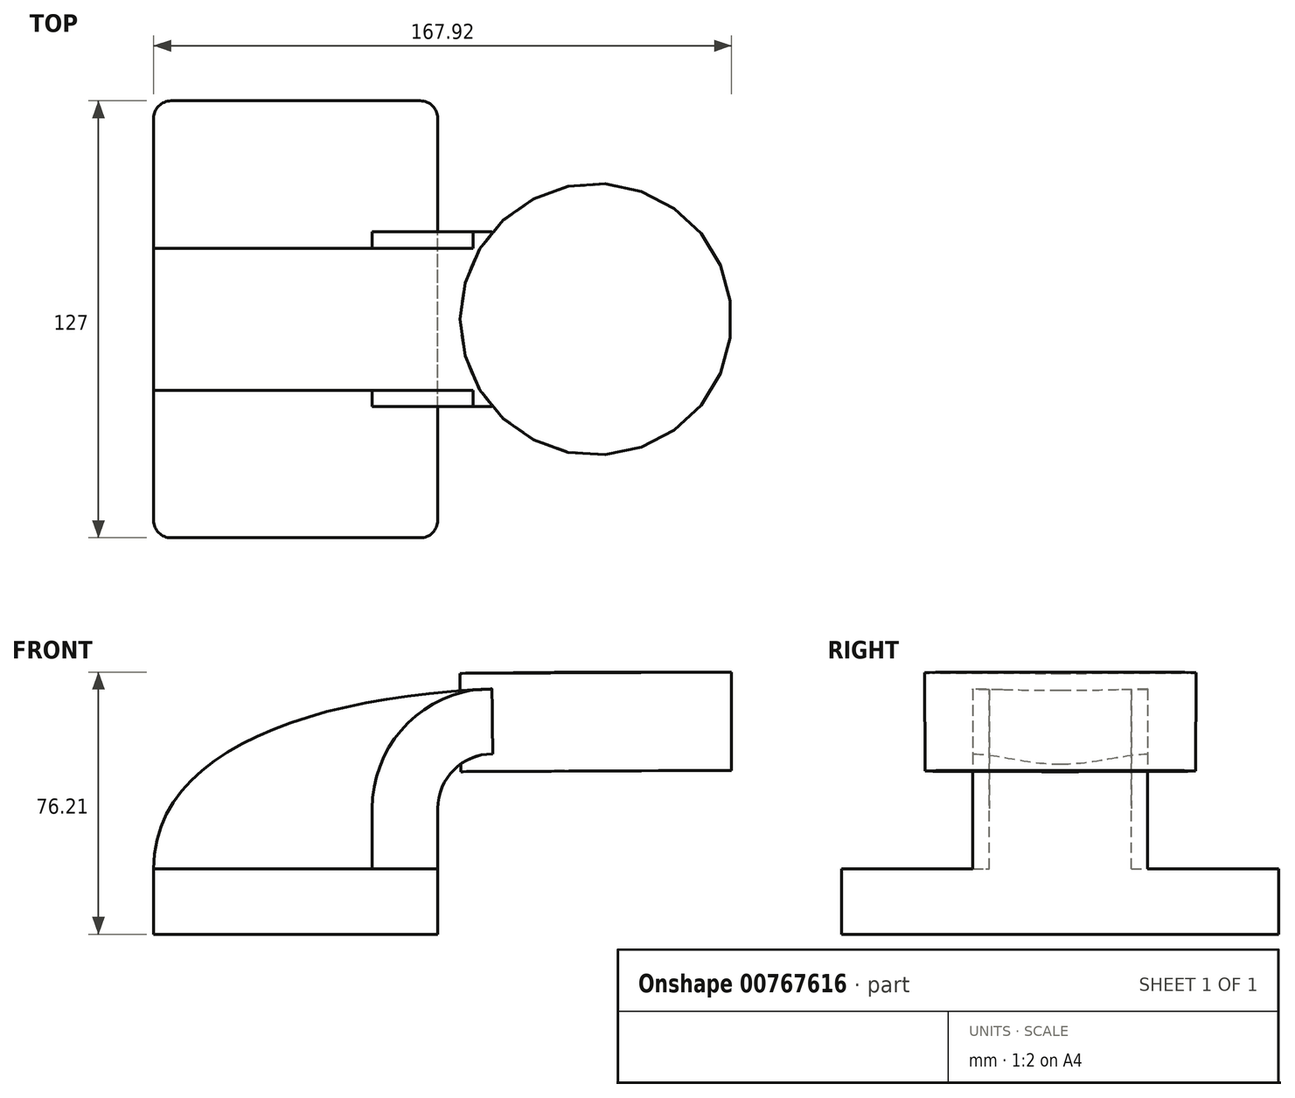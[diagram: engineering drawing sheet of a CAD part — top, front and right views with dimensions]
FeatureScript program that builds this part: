
annotation { "Feature Type Name" : "Feature", "Feature Type Description" : "" }
export const myFeature = defineFeature(function(context is Context, id is Id, definition is map)
    precondition{}
    {
        {
            var Q0;
            Q0=qCreatedBy(makeId("Front.planeOp"),FACE);
            var sketch = newSketch(context, id + "F0", { "sketchPlane" : qUnion([Q0])});
            skLineSegment(sketch, "E0.bottom", {"start": v(41.28, -9.52) * mm, "end": v(-41.28, -9.53) * mm});
            skLineSegment(sketch, "E0.top", {"start": v(41.28, 9.53) * mm, "end": v(-41.28, 9.53) * mm});
            skLineSegment(sketch, "E0.left", {"start": v(41.28, -9.52) * mm, "end": v(41.28, 9.53) * mm});
            skLineSegment(sketch, "E0.right", {"start": v(-41.28, -9.53) * mm, "end": v(-41.28, 9.53) * mm});
            skPoint(sketch, "E0.middle", {"position": v(0, 0) * mm});
            skLineSegment(sketch, "E1.bottom", {"start": v(75.84, 38.1) * mm, "end": v(126.64, 38.1) * mm});
            skLineSegment(sketch, "E1.top", {"start": v(75.84, 66.68) * mm, "end": v(126.64, 66.68) * mm});
            skLineSegment(sketch, "E1.left", {"start": v(75.84, 38.1) * mm, "end": v(75.84, 66.68) * mm});
            skLineSegment(sketch, "E1.right", {"start": v(126.64, 38.1) * mm, "end": v(126.64, 66.68) * mm});
            skPoint(sketch, "E1.middle", {"position": v(101.24, 52.39) * mm});
            skLineSegment(sketch, "E2", {"start": v(41.28, 9.53) * mm, "end": v(41.28, 27) * mm});
            skArc(sketch, "E3", {"start": v(41.27, 27) * mm, "mid": v(45.92, 38.23) * mm, "end": v(57.15, 42.88) * mm});
            skLineSegment(sketch, "E4", {"start": v(57.15, 42.88) * mm, "end": v(87.18, 42.88) * mm});
            skLineSegment(sketch, "E5.0", {"start": v(57.15, 61.93) * mm, "end": v(87.18, 61.93) * mm});
            skArc(sketch, "E5.1", {"start": v(22.23, 27) * mm, "mid": v(32.45, 51.7) * mm, "end": v(57.15, 61.93) * mm});
            skLineSegment(sketch, "E5.2", {"start": v(22.22, 9.53) * mm, "end": v(22.22, 27) * mm});
            skLineSegment(sketch, "E6", {"start": v(87.32, 38.1) * mm, "end": v(87.18, 66.68) * mm});
            skFitSpline(sketch, "E7", {"points": [v(-41.28, 9.52) * mm, v(72.17, 61.93) * mm], "startDerivative": vector(-0.11, 113.07) * mm, "endDerivative": vector(173.37, -2.18) * mm});
            skSolve(sketch);
        }
        {
            var Q0;
            Q0=makeQuery(id+"F0.imprint","IMPRINT",FACE,{"disambiguationData":[TD([[makeQuery(id+"F0.imprint","IMPRINT",EDGE,{"derivedFrom":sQuery(id+"F0.wireOp",EDGE,"E0.bottom")}),-1.0]])]});
            extrude(context, id + "F1", {"entities" : qUnion([Q0]), "endBound" : BoundingType.SYMMETRIC, "depth" : 127 * mm, "offsetDistance" : 25.4 * mm});
        }
        {
            var Q0;
            {var subQ1=sQuery(id+"F0.wireOp",EDGE,"E2");Q0=makeQuery(id+"F0.imprint","IMPRINT",FACE,{"disambiguationData":[TD([[makeQuery(id+"F0.imprint","IMPRINT",EDGE,{"derivedFrom":subQ1}),1.0]])]});}
            extrude(context, id + "F2", {"entities" : qUnion([Q0]), "operationType" : NewBodyOperationType.ADD, "endBound" : BoundingType.SYMMETRIC, "depth" : 50.8 * mm, "offsetDistance" : 25.4 * mm});
        }
        {
            var Q0;
            {var subQ3=sQuery(id+"F0.wireOp",EDGE,"E5.2");Q0=makeQuery(id+"F0.imprint","IMPRINT",FACE,{"disambiguationData":[TD([[makeQuery(id+"F0.imprint","IMPRINT",EDGE,{"derivedFrom":subQ3}),1.0]])]});}
            extrude(context, id + "F3", {"entities" : qUnion([Q0]), "operationType" : NewBodyOperationType.ADD, "endBound" : BoundingType.SYMMETRIC, "depth" : 41.27 * mm, "offsetDistance" : 25.4 * mm});
        }
        {
            var Q0;
            {var subQ0=sQuery(id+"F0.wireOp",EDGE,"E1.right");Q0=makeQuery(id+"F0.imprint","IMPRINT",FACE,{"disambiguationData":[TD([[makeQuery(id+"F0.imprint","IMPRINT",EDGE,{"derivedFrom":subQ0}),1.0]])]});}
            var Q1;
            Q1=sQuery(id+"F0.wireOp",EDGE,"E6");
            revolve(context, id + "F4", {"operationType" : NewBodyOperationType.ADD, "surfaceOperationType" : NewSurfaceOperationType.NEW, "entities" : qUnion([Q0]), "axis" : qUnion([Q1]), "revolveType" : RevolveType.FULL});
        }
        {
            var Q0;
            Q0=makeQuery(id+"F1.opExtrude","CAP_EDGE",EDGE,{"disambiguationData":[OSD([sQuery(id+"F0.wireOp",EDGE,"E0.left")])],"isStart":false});
            var Q1;
            Q1=makeQuery(id+"F1.opExtrude","CAP_EDGE",EDGE,{"disambiguationData":[OSD([sQuery(id+"F0.wireOp",EDGE,"E0.right")])],"isStart":false});
            var Q2;
            Q2=makeQuery(id+"F1.opExtrude","CAP_EDGE",EDGE,{"disambiguationData":[OSD([sQuery(id+"F0.wireOp",EDGE,"E0.left")])],"isStart":true});
            var Q3;
            Q3=makeQuery(id+"F1.opExtrude","CAP_EDGE",EDGE,{"disambiguationData":[OSD([sQuery(id+"F0.wireOp",EDGE,"E0.right")])],"isStart":true});
            fillet(context, id + "F5", {"entities" : qUnion([Q0, Q1, Q2, Q3]), "radius" : 5.08 * mm, "tangentPropagation" : true, "allowEdgeOverflow" : false});
        }
    });
